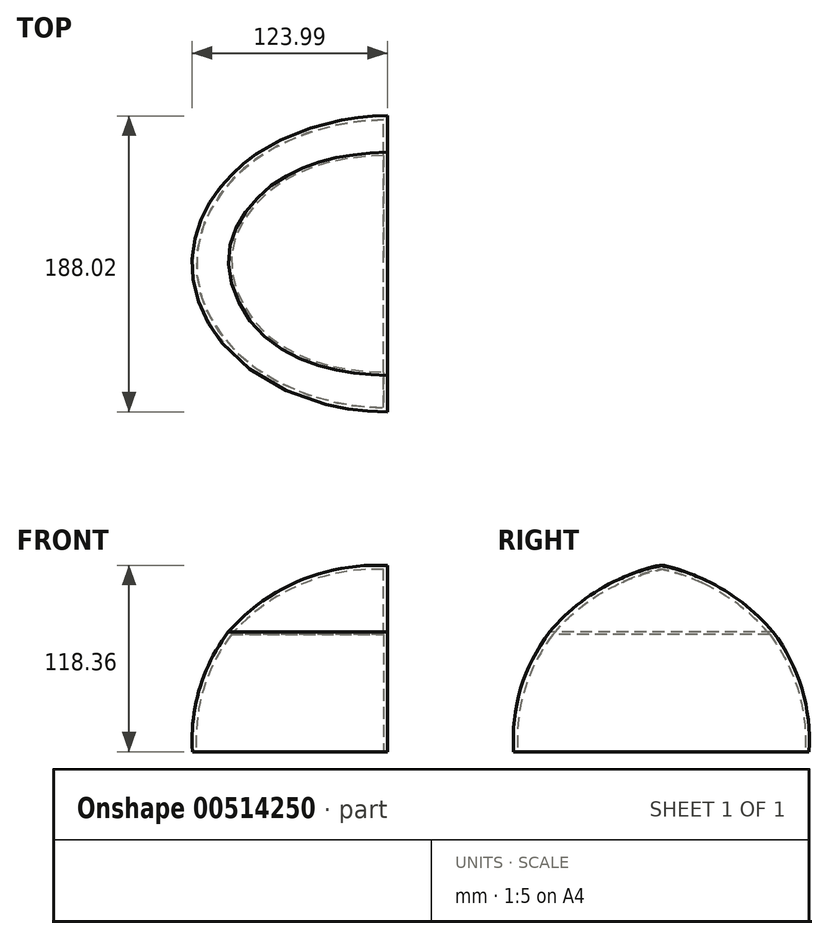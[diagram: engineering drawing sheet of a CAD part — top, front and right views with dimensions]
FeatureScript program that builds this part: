
annotation { "Feature Type Name" : "Feature", "Feature Type Description" : "" }
export const myFeature = defineFeature(function(context is Context, id is Id, definition is map)
    precondition{}
    {
        {
            var Q0;
            Q0=qCreatedBy(makeId("Top.planeOp"),FACE);
            var sketch = newSketch(context, id + "F0", { "sketchPlane" : qUnion([Q0])});
            skLineSegment(sketch, "E0", {"start": v(0, 0) * mm, "end": v(0, 93.75) * mm, "construction": true});
            skLineSegment(sketch, "E1", {"start": v(0, 0) * mm, "end": v(-123.73, 0) * mm, "construction": true});
            skLineSegment(sketch, "E2", {"start": v(0, 0) * mm, "end": v(0, -93.81) * mm, "construction": true});
            skLineSegment(sketch, "E3", {"start": v(0, 0) * mm, "end": v(-98.41, 56.82) * mm, "construction": true});
            skLineSegment(sketch, "E4", {"start": v(0, 0) * mm, "end": v(-49.59, 85.89) * mm, "construction": true});
            skLineSegment(sketch, "E5.MirrorCS", {"start": v(0, 0) * mm, "end": v(-98.41, -56.82) * mm, "construction": true});
            skLineSegment(sketch, "E6.MirrorCS", {"start": v(0, 0) * mm, "end": v(-49.59, -85.89) * mm, "construction": true});
            skEllipticalArc(sketch, "E7", {});
            const initialGuessF0  = {"E7": [0, 0, -1, 0, 0.1237266453872342, 0.09374764666870355, 4.71238898038469, 1.5707963267948966]};
            skSetInitialGuess(sketch, initialGuessF0);
            skSolve(sketch);
        }
        {
            var Q0;
            Q0=qCreatedBy(makeId("Front.planeOp"),FACE);
            var sketch = newSketch(context, id + "F1", { "sketchPlane" : qUnion([Q0])});
            skArc(sketch, "E8", {"start": v(-101, 75.93) * mm, "mid": v(-119.26, 40.03) * mm, "end": v(-123.73, 0) * mm});
            skArc(sketch, "E9", {"start": v(0, 118.14) * mm, "mid": v(-55.4, 108.74) * mm, "end": v(-101, 75.93) * mm});
            skLineSegment(sketch, "E10", {"start": v(0, 0) * mm, "end": v(0, 118.14) * mm});
            skLineSegment(sketch, "E11", {"start": v(-123.73, 0) * mm, "end": v(0, 0) * mm});
            skSolve(sketch);
        }
        {
            var Q0;
            Q0=sQuery(id+"F0.wireOp",EDGE,"E4");
            var Q1;
            Q1=qCreatedBy(makeId("Front.planeOp"),FACE);
            cPlane(context, id + "F2", {"entities" : qUnion([Q0, Q1]), "cplaneType" : CPlaneType.LINE_ANGLE, "offset" : 25 * mm, "angle" : 0 * degree, "width" : 150 * mm, "height" : 150 * mm});
        }
        {
            var Q0;
            Q0=sQuery(id+"F0.wireOp",EDGE,"E3");
            var Q1;
            Q1=qCreatedBy(makeId("Front.planeOp"),FACE);
            cPlane(context, id + "F3", {"entities" : qUnion([Q0, Q1]), "cplaneType" : CPlaneType.LINE_ANGLE, "offset" : 25 * mm, "angle" : 0 * degree, "width" : 150 * mm, "height" : 150 * mm});
        }
        {
            var Q0;
            Q0=sQuery(id+"F0.wireOp",EDGE,"E5.MirrorCS");
            cPlane(context, id + "F4", {"entities" : qUnion([Q0]), "cplaneType" : CPlaneType.LINE_ANGLE, "offset" : 25 * mm, "angle" : 0 * degree, "width" : 150 * mm, "height" : 150 * mm});
        }
        {
            var Q0;
            Q0=sQuery(id+"F0.wireOp",EDGE,"E6.MirrorCS");
            var Q1;
            Q1=qCreatedBy(makeId("Front.planeOp"),FACE);
            cPlane(context, id + "F5", {"entities" : qUnion([Q0, Q1]), "cplaneType" : CPlaneType.LINE_ANGLE, "offset" : 25 * mm, "angle" : 0 * degree, "width" : 150 * mm, "height" : 150 * mm});
        }
        {
            var Q0;
            Q0=qCreatedBy(id+"F3.planeOp",FACE);
            var sketch = newSketch(context, id + "F6", { "sketchPlane" : qUnion([Q0])});
            skLineSegment(sketch, "E12", {"start": v(0, 0) * mm, "end": v(0, 118.14) * mm});
            skArc(sketch, "E13.MirrorCS", {"start": v(0, 118.14) * mm, "mid": v(49.9, 106.6) * mm, "end": v(90.92, 75.93) * mm});
            skArc(sketch, "E14.MirrorCS", {"start": v(90.92, 75.93) * mm, "mid": v(109.18, 40.03) * mm, "end": v(113.64, 0) * mm});
            skLineSegment(sketch, "E15.MirrorCS", {"start": v(113.64, 0) * mm, "end": v(0, 0) * mm});
            skSolve(sketch);
        }
        {
            var Q0;
            Q0=qCreatedBy(id+"F2.planeOp",FACE);
            var sketch = newSketch(context, id + "F7", { "sketchPlane" : qUnion([Q0])});
            skLineSegment(sketch, "E16", {"start": v(0, 0) * mm, "end": v(0, 118.14) * mm});
            skArc(sketch, "E17.MirrorCS", {"start": v(0, 118.14) * mm, "mid": v(42.05, 103.96) * mm, "end": v(76.45, 75.93) * mm});
            skArc(sketch, "E18.MirrorCS", {"start": v(76.45, 75.93) * mm, "mid": v(94.71, 40.03) * mm, "end": v(99.18, 0) * mm});
            skLineSegment(sketch, "E19.MirrorCS", {"start": v(99.18, 0) * mm, "end": v(0, 0) * mm});
            skSolve(sketch);
        }
        {
            var Q0;
            Q0=qCreatedBy(makeId("Right.planeOp"),FACE);
            var sketch = newSketch(context, id + "F8", { "sketchPlane" : qUnion([Q0])});
            skArc(sketch, "E20", {"start": v(-71.03, 75.93) * mm, "mid": v(-89.29, 40.03) * mm, "end": v(-93.75, 0) * mm});
            skArc(sketch, "E21", {"start": v(0, 118.14) * mm, "mid": v(-39.12, 103.1) * mm, "end": v(-71.03, 75.93) * mm});
            skLineSegment(sketch, "E22", {"start": v(0, 0) * mm, "end": v(0, 118.14) * mm});
            skLineSegment(sketch, "E23", {"start": v(-93.75, 0) * mm, "end": v(0, 0) * mm});
            skArc(sketch, "E24.MirrorCS", {"start": v(0, 118.14) * mm, "mid": v(39.12, 103.1) * mm, "end": v(71.03, 75.93) * mm});
            skArc(sketch, "E25.MirrorCS", {"start": v(71.03, 75.93) * mm, "mid": v(89.29, 40.03) * mm, "end": v(93.75, 0) * mm});
            skLineSegment(sketch, "E26.MirrorCS", {"start": v(93.75, 0) * mm, "end": v(0, 0) * mm});
            skSolve(sketch);
        }
        {
            var Q0;
            Q0=qCreatedBy(id+"F4.planeOp",FACE);
            var sketch = newSketch(context, id + "F9", { "sketchPlane" : qUnion([Q0])});
            skArc(sketch, "E27", {"start": v(-90.92, 75.93) * mm, "mid": v(-109.18, 40.03) * mm, "end": v(-113.64, 0) * mm});
            skArc(sketch, "E28", {"start": v(0, 118.14) * mm, "mid": v(-49.9, 106.6) * mm, "end": v(-90.92, 75.93) * mm});
            skLineSegment(sketch, "E29", {"start": v(0, 0) * mm, "end": v(0, 118.14) * mm});
            skLineSegment(sketch, "E30", {"start": v(-113.64, 0) * mm, "end": v(0, 0) * mm});
            skSolve(sketch);
        }
        {
            var Q0;
            Q0=qCreatedBy(id+"F5.planeOp",FACE);
            var sketch = newSketch(context, id + "F10", { "sketchPlane" : qUnion([Q0])});
            skLineSegment(sketch, "E31", {"start": v(0, 0) * mm, "end": v(0, 118.14) * mm});
            skArc(sketch, "E32.MirrorCS", {"start": v(0, 118.14) * mm, "mid": v(42.05, 103.96) * mm, "end": v(76.45, 75.93) * mm});
            skArc(sketch, "E33.MirrorCS", {"start": v(76.45, 75.93) * mm, "mid": v(94.71, 40.03) * mm, "end": v(99.18, 0) * mm});
            skLineSegment(sketch, "E34.MirrorCS", {"start": v(99.18, 0) * mm, "end": v(0, 0) * mm});
            skSolve(sketch);
        }
        {
            var Q0;
            Q0=makeQuery(id+"F8.imprint","IMPRINT",FACE,{"disambiguationData":[TD([[makeQuery(id+"F8.imprint","IMPRINT",EDGE,{"derivedFrom":sQuery(id+"F8.wireOp",EDGE,"E22")}),-1.0]])]});
            var Q1;
            Q1=makeQuery(id+"F7.imprint","IMPRINT",FACE,{"disambiguationData":[TD([[makeQuery(id+"F7.imprint","IMPRINT",EDGE,{"derivedFrom":sQuery(id+"F7.wireOp",EDGE,"E16")}),-1.0]])]});
            var Q2;
            Q2=makeQuery(id+"F6.imprint","IMPRINT",FACE,{"disambiguationData":[TD([[makeQuery(id+"F6.imprint","IMPRINT",EDGE,{"derivedFrom":sQuery(id+"F6.wireOp",EDGE,"E12")}),-1.0]])]});
            var Q3;
            Q3=makeQuery(id+"F1.imprint","IMPRINT",FACE,{"disambiguationData":[TD([[makeQuery(id+"F1.imprint","IMPRINT",EDGE,{"derivedFrom":sQuery(id+"F1.wireOp",EDGE,"E8")}),1.0]])]});
            var Q4;
            Q4=makeQuery(id+"F9.imprint","IMPRINT",FACE,{"disambiguationData":[TD([[makeQuery(id+"F9.imprint","IMPRINT",EDGE,{"derivedFrom":sQuery(id+"F9.wireOp",EDGE,"E27")}),1.0]])]});
            var Q5;
            Q5=makeQuery(id+"F10.imprint","IMPRINT",FACE,{"disambiguationData":[TD([[makeQuery(id+"F10.imprint","IMPRINT",EDGE,{"derivedFrom":sQuery(id+"F10.wireOp",EDGE,"E31")}),-1.0]])]});
            var Q6;
            Q6=makeQuery(id+"F8.imprint","IMPRINT",FACE,{"disambiguationData":[TD([[makeQuery(id+"F8.imprint","IMPRINT",EDGE,{"derivedFrom":sQuery(id+"F8.wireOp",EDGE,"E20")}),1.0]])]});
            var Q7;
            Q7=sQuery(id+"F0.wireOp",EDGE,"E7");
            loft(context, id + "F11", {"addGuides" : true, "sheetProfilesArray" : [{ "sheetProfileEntities" : qUnion([Q0]) }, { "sheetProfileEntities" : qUnion([Q1]) }, { "sheetProfileEntities" : qUnion([Q2]) }, { "sheetProfileEntities" : qUnion([Q3]) }, { "sheetProfileEntities" : qUnion([Q4]) }, { "sheetProfileEntities" : qUnion([Q5]) }, { "sheetProfileEntities" : qUnion([Q6]) }], "guidesArray" : [{ "guideEntities" : qUnion([Q7]), "guideDerivativeType" : LoftGuideDerivativeType.DEFAULT, "guideDerivativeMagnitude" : 1 }]});
        }
        {
            var Q0;
            Q0=makeQuery(id+"F11.opLoft","SWEPT_FACE",FACE,{"disambiguationData":[OSD([sQuery(id+"F0.wireOp",EDGE,"E7"),sQuery(id+"F7.wireOp",EDGE,"E16"),sQuery(id+"F7.wireOp",EDGE,"E19.MirrorCS"),sQuery(id+"F8.wireOp",EDGE,"E22"),sQuery(id+"F8.wireOp",EDGE,"E23"),sQuery(id+"F8.wireOp",EDGE,"E26.MirrorCS")])]});
            shell(context, id + "F12", {"entities" : qUnion([Q0]), "thickness" : 2.5 * mm});
        }
    });
